# Revit family: AIRTECNICS_AIR CURTAIN_ROTOWIND_DX_(MIDEA) - (False Ceiling Mounting)_00
name_source: partatom
category: Mechanical Equipment
revit_build: Autodesk Revit 2016 (Build: 20150714_1515(x64)
units: mm (PartAtom-declared; Revit-internal decimal feet)

## family parameters
Always vertical = Yes
Cut with Voids When Loaded = No
OmniClass Number = 23.75.70.21.17
OmniClass Title = Air Curtains
Part Type = Normal
Room Calculation Point = No
Round Connector Dimension = Use Diameter
Shared = No
Work Plane-Based = No

## types (1)
- ROTOWIND ECG DX-MD - (False Ceiling Mounting)
    BIMETRICAL = http://www.bimetrical.com
    BIMETRICAL Category = Coil
    Cable = CB7
    DX 1:1 = Yes
    Depth = 360 mm
    EC = Yes
    Family Version = 1.0
    Fans Stage = 5
    Frequency = 50 Hz
    G = Yes
    Height = 285 mm
    IfcExportAs = IfcCoilType
    IfcExportType = DXCOOLINGCOIL
    Manufacturer = AIRTECNICS
    Model = Air curtain Rotowind ECG DX MD
    Name_Lookup_Data = ROTOWIND_(DX)_MD_Data_Lookup
    Name_Lookup_Data2 = ROTOWIND_(DX)_MD_Mainfolds_Lookup
    Name_Lookup_Data3 = ROTOWIND_(DX)_MD_ExpValve_Lookup
    Name_Lookup_Ref = ROTOWIND_(DX)_MD_Ref_Lookup
    Name_Lookup_Ref_EU = ROTOWIND_(DX)_MD_Ref_EU_Lookup
    Remote Control = AIR-IR
    Review Date = 02/19
    Revit Version = Revit 2016 - English
    Type Comments = Energy saving heat pump air curtain: Up to 70% reduction in costs and CO2 emissions (heating mode).
Specially designed to be installed in all type of revolving doors. Two possible layouts, tailored dimensions.
Self-supporting casing construction made of galvanized steel plate, finished in structural epoxy-polyester painting white colour RAL9016 as standard. Other colours or stainless steel are available on request. 
Large faceted inlet grille avoiding intensive maintenance. 
Circular anodized aluminium outlet vanes, airfoil shaped.
Double-inlet centrifugal fans driven by an external rotor motor and low noise level. 5-speed selector. EC models assembled with very low consumption efficiency fans. 
Includes only heating direct expansion coil with installed temperature sensors. Under request it can be modified to work in cooling and heating mode (not recomended) with optional condensate water pump.
Includes Plug&Play control with 7m RJ45 cable and infrared remote control. 
Ready to connect to MIDEA Inverter outdoor heat pump unit (R410A) with expansion valve, not included, the customer should purchase it.
Requires  DX Interface KIT adapted for air curtain and  programmable control, please consult.
    Type Image = <None>
    URL = https://www.airtecnics.com
    URL_Datasheet = https://www.airtecnics.com
    URL_Manufacturer = https://www.airtecnics.com
    · HEATING · = -/ Select Heating /-
